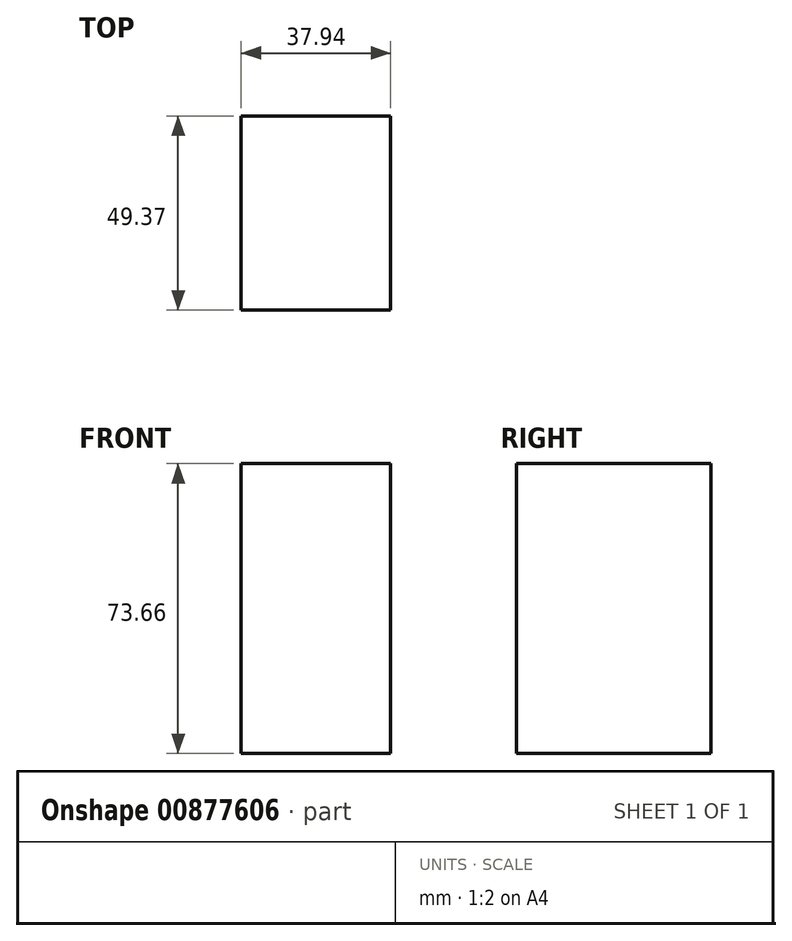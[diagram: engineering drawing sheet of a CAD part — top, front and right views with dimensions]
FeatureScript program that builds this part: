
annotation { "Feature Type Name" : "Feature", "Feature Type Description" : "" }
export const myFeature = defineFeature(function(context is Context, id is Id, definition is map)
    precondition{}
    {
        {
            var Q0;
            Q0=qCreatedBy(makeId("Top.planeOp"),FACE);
            var sketch = newSketch(context, id + "F0", { "sketchPlane" : qUnion([Q0])});
            skLineSegment(sketch, "E0.bottom", {"start": v(0, 0) * mm, "end": v(37.94, 0) * mm});
            skLineSegment(sketch, "E0.top", {"start": v(0, 49.37) * mm, "end": v(37.94, 49.37) * mm});
            skLineSegment(sketch, "E0.left", {"start": v(0, 0) * mm, "end": v(0, 49.37) * mm});
            skLineSegment(sketch, "E0.right", {"start": v(37.94, 0) * mm, "end": v(37.94, 49.37) * mm});
            skSolve(sketch);
        }
        {
            var Q0;
            Q0=makeQuery(id+"F0.imprint","IMPRINT",FACE,{"disambiguationData":[TD([[makeQuery(id+"F0.imprint","IMPRINT",EDGE,{"derivedFrom":sQuery(id+"F0.wireOp",EDGE,"E0.bottom")}),1.0]])]});
            extrude(context, id + "F1", {"entities" : qUnion([Q0]), "depth" : 73.66 * mm, "offsetDistance" : 25.4 * mm});
        }
    });
